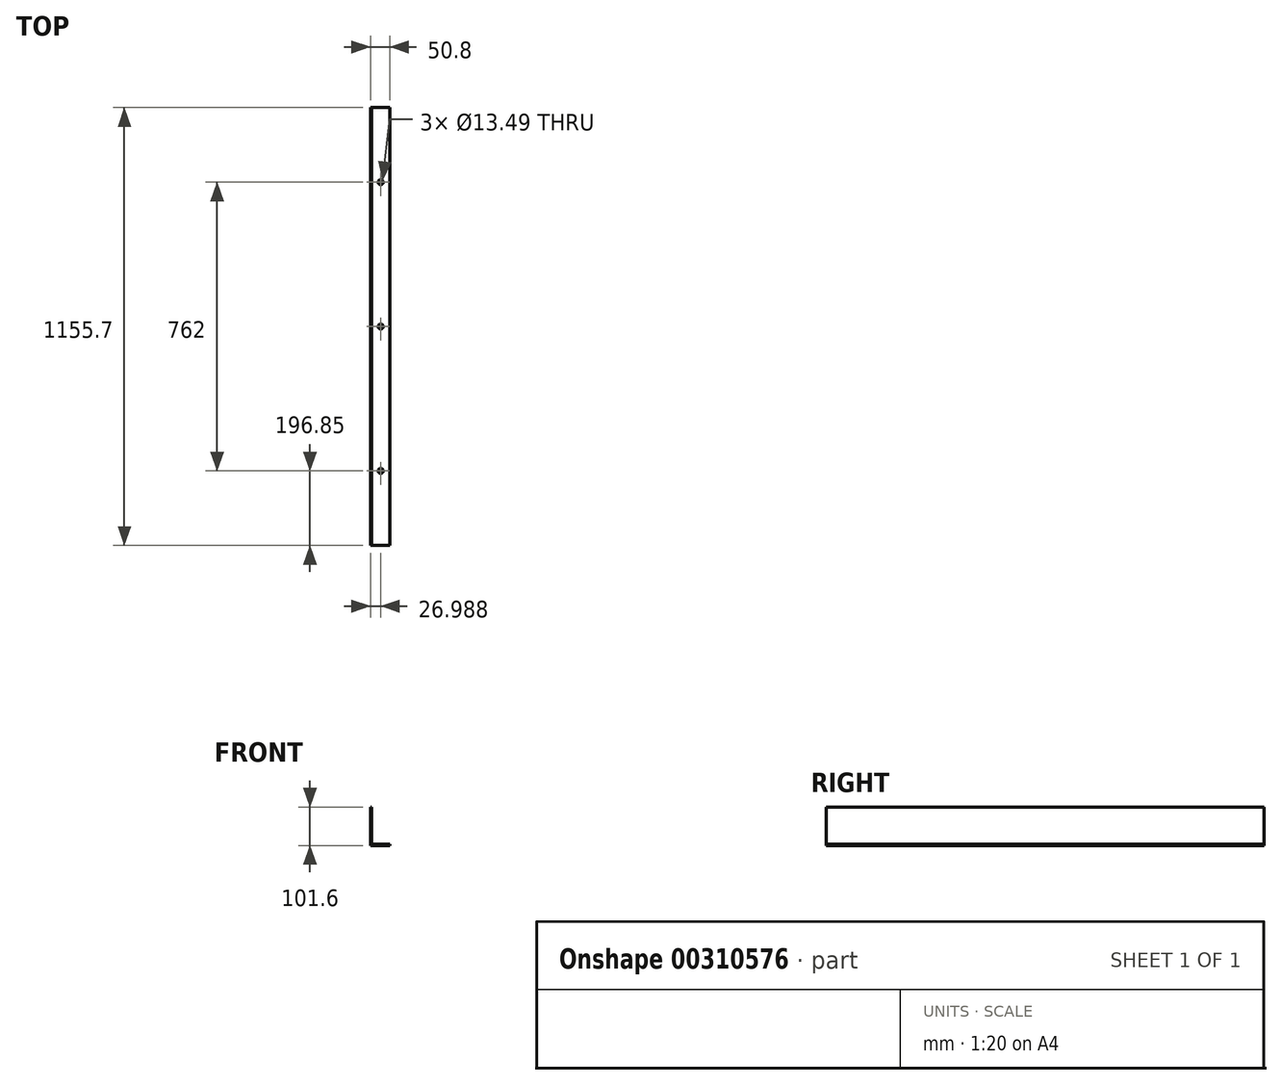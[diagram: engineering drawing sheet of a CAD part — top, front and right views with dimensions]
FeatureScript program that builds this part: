
annotation { "Feature Type Name" : "Feature", "Feature Type Description" : "" }
export const myFeature = defineFeature(function(context is Context, id is Id, definition is map)
    precondition{}
    {
        {
            var Q0;
            Q0=qCreatedBy(makeId("Front.planeOp"),FACE);
            var sketch = newSketch(context, id + "F0", { "sketchPlane" : qUnion([Q0])});
            skLineSegment(sketch, "E0", {"start": v(0, 0) * mm, "end": v(0, 101.6) * mm});
            skLineSegment(sketch, "E1", {"start": v(0, 101.6) * mm, "end": v(3.17, 101.6) * mm});
            skLineSegment(sketch, "E2", {"start": v(3.18, 101.6) * mm, "end": v(3.18, 3.18) * mm});
            skLineSegment(sketch, "E3", {"start": v(3.17, 3.17) * mm, "end": v(50.8, 3.17) * mm});
            skLineSegment(sketch, "E4", {"start": v(50.8, 3.17) * mm, "end": v(50.8, 0) * mm});
            skLineSegment(sketch, "E5", {"start": v(50.8, 0) * mm, "end": v(0, 0) * mm});
            skSolve(sketch);
        }
        {
            var Q0;
            Q0 = qSketchRegion(id + "F0", true);
            extrude(context, id + "F1", {"entities" : qUnion([Q0]), "depth" : 1155.7 * mm});
        }
        {
            var Q0;
            Q0=makeQuery(id+"F1.opExtrude","SWEPT_FACE",FACE,{"disambiguationData":[OSD([sQuery(id+"F0.wireOp",EDGE,"E3")])]});
            var sketch = newSketch(context, id + "F2", { "sketchPlane" : qUnion([Q0])});
            skPoint(sketch, "E6", {"position": v(26.99, -577.85) * mm});
            skPoint(sketch, "E6.positionSnap0", {"position": v(26.99, 0) * mm});
            skPoint(sketch, "E6.positionSnap1", {"position": v(50.8, -577.85) * mm});
            skPoint(sketch, "E7", {"position": v(26.99, -196.85) * mm});
            skPoint(sketch, "E8", {"position": v(26.99, -958.85) * mm});
            skSolve(sketch);
        }
        {
            var Q0;
            Q0=sQuery(id+"F2.wireOp",VERTEX,"E6");
            var Q1;
            Q1=sQuery(id+"F2.wireOp",VERTEX,"E7");
            var Q2;
            Q2=sQuery(id+"F2.wireOp",VERTEX,"E8");
            var Q3;
            Q3=makeQuery(id+"F1.opExtrude","SWEPT_BODY",BODY,{"disambiguationData":[OSD([sQuery(id+"F0.wireOp",EDGE,"E0"),sQuery(id+"F0.wireOp",EDGE,"E1"),sQuery(id+"F0.wireOp",EDGE,"E2"),sQuery(id+"F0.wireOp",EDGE,"E3"),sQuery(id+"F0.wireOp",EDGE,"E4"),sQuery(id+"F0.wireOp",EDGE,"E5")])]});
            hole(context, id + "F3", {"style" : HoleStyle.SIMPLE, "endStyle" : HoleEndStyle.THROUGH, "standardTappedOrClearance" : lookupTablePath({ "standard" : "ANSI", "fit" : "Normal (ASME)", "size" : "1/2", "type" : "Clearance" }), "standardBlindInLast" : lookupTablePath({ "fit" : "Free", "standard" : "ANSI", "size" : "1/2", "type" : "Clearance" }), "holeDiameter" : 13.5 * mm, "isTappedThrough" : true, "tappedDepth" : 21.59 * mm, "tapClearance" : 3, "startFromSketch" : true, "locations" : qUnion([Q0, Q1, Q2]), "scope" : qUnion([Q3])});
        }
    });
